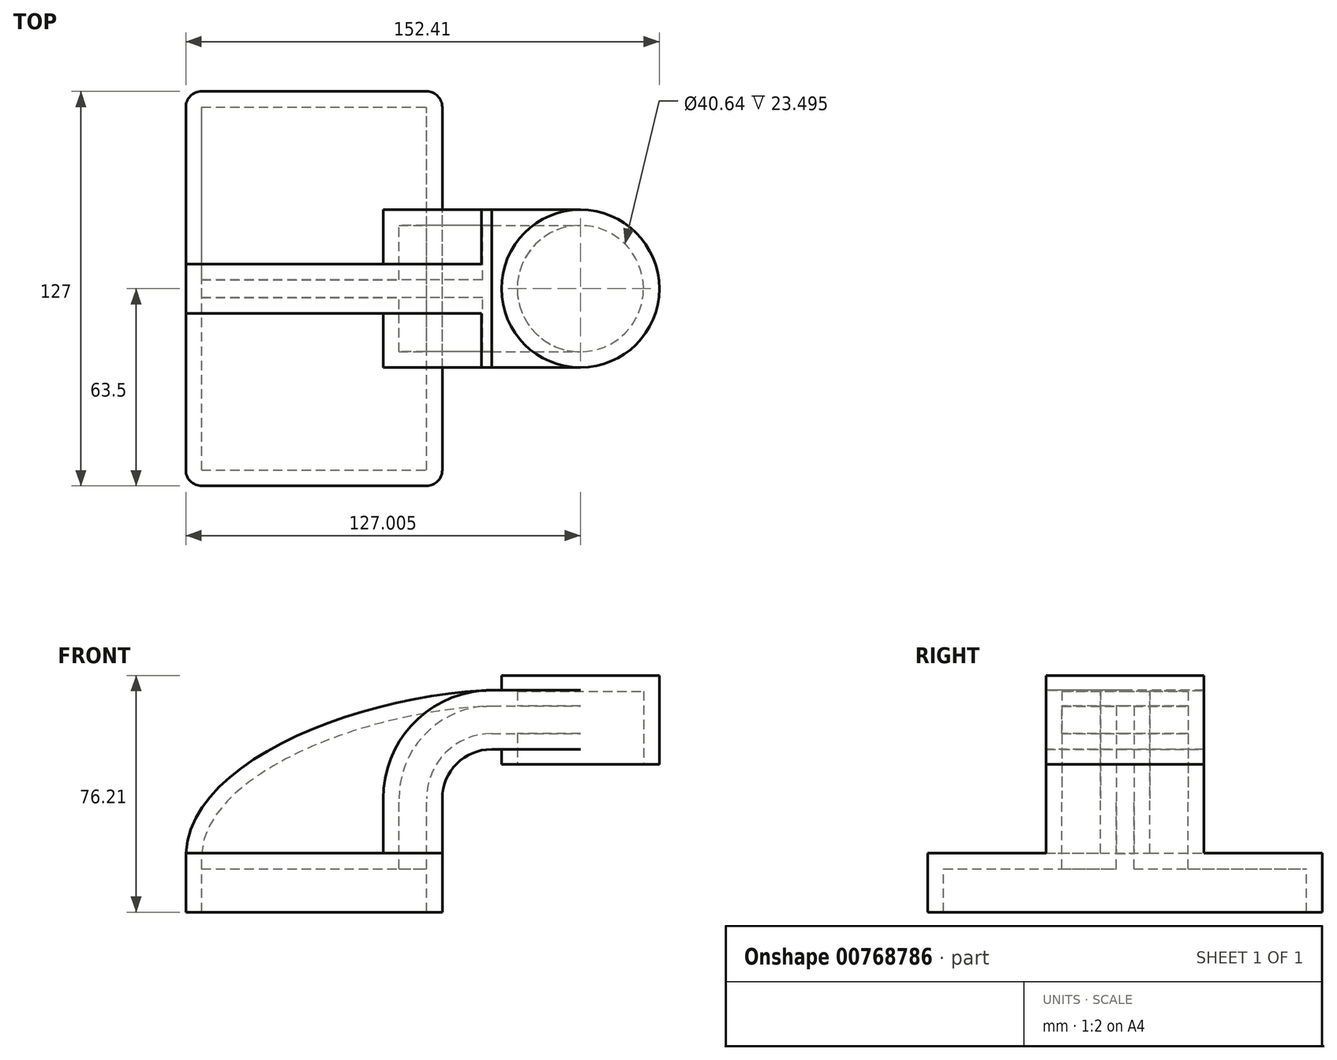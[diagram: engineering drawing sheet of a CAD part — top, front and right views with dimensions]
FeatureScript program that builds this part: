
annotation { "Feature Type Name" : "Feature", "Feature Type Description" : "" }
export const myFeature = defineFeature(function(context is Context, id is Id, definition is map)
    precondition{}
    {
        {
            var Q0;
            Q0=qCreatedBy(makeId("Front.planeOp"),FACE);
            var sketch = newSketch(context, id + "F0", { "sketchPlane" : qUnion([Q0])});
            skLineSegment(sketch, "E0.rect.bottom", {"start": v(-41.28, 9.52) * mm, "end": v(41.28, 9.52) * mm});
            skLineSegment(sketch, "E0.rect.top", {"start": v(-41.28, -9.52) * mm, "end": v(41.28, -9.52) * mm});
            skLineSegment(sketch, "E0.rect.left", {"start": v(-41.28, 9.52) * mm, "end": v(-41.28, -9.52) * mm});
            skLineSegment(sketch, "E0.rect.right", {"start": v(41.28, 9.52) * mm, "end": v(41.28, -9.52) * mm});
            skPoint(sketch, "E0.rect.middle", {"position": v(0, 0) * mm});
            skLineSegment(sketch, "E1", {"start": v(41.28, 9.52) * mm, "end": v(41.28, 27) * mm});
            skArc(sketch, "E2", {"start": v(41.28, 27) * mm, "mid": v(45.92, 38.23) * mm, "end": v(57.15, 42.88) * mm});
            skLineSegment(sketch, "E3", {"start": v(57.15, 42.88) * mm, "end": v(85.72, 42.88) * mm});
            skLineSegment(sketch, "E4.rect.bottom", {"start": v(60.32, 38.1) * mm, "end": v(111.12, 38.1) * mm});
            skLineSegment(sketch, "E4.rect.top", {"start": v(60.32, 66.68) * mm, "end": v(111.12, 66.68) * mm});
            skLineSegment(sketch, "E4.rect.left", {"start": v(60.32, 38.1) * mm, "end": v(60.32, 66.68) * mm});
            skLineSegment(sketch, "E4.rect.right", {"start": v(111.13, 38.1) * mm, "end": v(111.12, 66.68) * mm});
            skPoint(sketch, "E4.rect.middle", {"position": v(85.72, 52.39) * mm});
            skLineSegment(sketch, "E5.0", {"start": v(57.15, 61.93) * mm, "end": v(85.72, 61.93) * mm});
            skArc(sketch, "E5.1", {"start": v(22.23, 27) * mm, "mid": v(32.45, 51.7) * mm, "end": v(57.15, 61.93) * mm});
            skLineSegment(sketch, "E5.2", {"start": v(22.23, 9.52) * mm, "end": v(22.23, 27) * mm});
            skLineSegment(sketch, "E6", {"start": v(85.72, 38.1) * mm, "end": v(85.72, 66.68) * mm});
            skFitSpline(sketch, "E7", {"points": [v(-41.28, 9.53) * mm, v(57.15, 61.93) * mm], "startDerivative": vector(5.2, 92.34) * mm, "endDerivative": vector(120.92, 4.22) * mm});
            skSolve(sketch);
        }
        {
            var Q0;
            Q0=makeQuery(id+"F0.imprint","IMPRINT",FACE,{"disambiguationData":[TD([[makeQuery(id+"F0.imprint","IMPRINT",EDGE,{"derivedFrom":sQuery(id+"F0.wireOp",EDGE,"E0.rect.top")}),1.0]])]});
            extrude(context, id + "F1", {"entities" : qUnion([Q0]), "endBound" : BoundingType.SYMMETRIC, "depth" : 127 * mm});
        }
        {
            var Q0;
            {var subQ9=sQuery(id+"F0.wireOp",EDGE,"E1");Q0=makeQuery(id+"F0.imprint","IMPRINT",FACE,{"disambiguationData":[TD([[makeQuery(id+"F0.imprint","IMPRINT",EDGE,{"derivedFrom":subQ9}),1.0]])]});}
            var Q1;
            {var subQ0=sQuery(id+"F0.wireOp",EDGE,"E6");var subQ1=sQuery(id+"F0.wireOp",EDGE,"E3");var subQ2=makeQuery(id+"F0.imprint","INTERSECT",VERTEX,{"derivedFrom":[subQ1,subQ0]});Q1=makeQuery(id+"F0.imprint","IMPRINT",FACE,{"disambiguationData":[TD([[makeQuery(id+"F0.imprint","IMPRINT",EDGE,{"disambiguationData":[TD([[subQ2,1.0]])],"derivedFrom":subQ1}),1.0]])]});}
            extrude(context, id + "F2", {"entities" : qUnion([Q0, Q1]), "operationType" : NewBodyOperationType.ADD, "endBound" : BoundingType.SYMMETRIC, "depth" : 50.8 * mm});
        }
        {
            var Q0;
            {var subQ3=sQuery(id+"F0.wireOp",EDGE,"E5.2");Q0=makeQuery(id+"F0.imprint","IMPRINT",FACE,{"disambiguationData":[TD([[makeQuery(id+"F0.imprint","IMPRINT",EDGE,{"derivedFrom":subQ3}),1.0]])]});}
            extrude(context, id + "F3", {"entities" : qUnion([Q0]), "operationType" : NewBodyOperationType.ADD, "endBound" : BoundingType.SYMMETRIC, "depth" : 15.88 * mm});
        }
        {
            var Q0;
            {var subQ5=sQuery(id+"F0.wireOp",EDGE,"E4.rect.right");Q0=makeQuery(id+"F0.imprint","IMPRINT",FACE,{"disambiguationData":[TD([[makeQuery(id+"F0.imprint","IMPRINT",EDGE,{"derivedFrom":subQ5}),1.0]])]});}
            var Q1;
            Q1=sQuery(id+"F0.wireOp",EDGE,"E6");
            revolve(context, id + "F4", {"operationType" : NewBodyOperationType.ADD, "entities" : qUnion([Q0]), "axis" : qUnion([Q1]), "revolveType" : RevolveType.FULL});
        }
        {
            var Q0;
            Q0=makeQuery(id+"F1.opExtrude","CAP_EDGE",EDGE,{"disambiguationData":[OSD([sQuery(id+"F0.wireOp",EDGE,"E0.rect.right")])],"isStart":false});
            var Q1;
            Q1=makeQuery(id+"F1.opExtrude","CAP_EDGE",EDGE,{"disambiguationData":[OSD([sQuery(id+"F0.wireOp",EDGE,"E0.rect.left")])],"isStart":false});
            var Q2;
            Q2=makeQuery(id+"F1.opExtrude","CAP_EDGE",EDGE,{"disambiguationData":[OSD([sQuery(id+"F0.wireOp",EDGE,"E0.rect.right")])],"isStart":true});
            var Q3;
            Q3=makeQuery(id+"F1.opExtrude","CAP_EDGE",EDGE,{"disambiguationData":[OSD([sQuery(id+"F0.wireOp",EDGE,"E0.rect.left")])],"isStart":true});
            fillet(context, id + "F5", {"entities" : qUnion([Q0, Q1, Q2, Q3]), "radius" : 5.08 * mm, "tangentPropagation" : true, "allowEdgeOverflow" : false});
        }
        {
            var Q0;
            Q0=makeQuery(id+"F1.opExtrude","SWEPT_FACE",FACE,{"disambiguationData":[OSD([sQuery(id+"F0.wireOp",EDGE,"E0.rect.top")])]});
            var Q1;
            Q1=makeQuery(id+"F4.opRevolve","SWEPT_FACE",FACE,{"disambiguationData":[OSD([sQuery(id+"F0.wireOp",EDGE,"E4.rect.bottom")])]});
            shell(context, id + "F6", {"entities" : qUnion([Q0, Q1]), "thickness" : 5.08 * mm});
        }
    });
